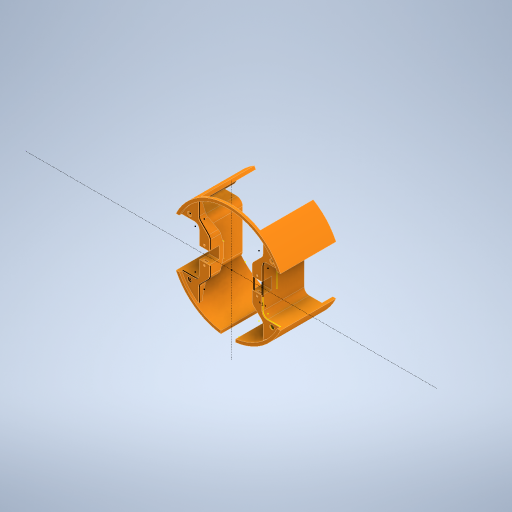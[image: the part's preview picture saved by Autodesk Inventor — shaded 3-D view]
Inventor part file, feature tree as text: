
AUTODESK INVENTOR PART (.ipt)
format: ipt  version: 2023.1 (Build 271208000, 208)  size: 742,400 bytes
history: native  units: mm
features: extrude x13, sketch x10, chamfer x6, projected_geometry x4, other x1, fillet x1, mirror x1
ambient origin geometry x8: Origin, YZ Plane, XZ Plane, XY Plane, X Axis, Y Axis, Z Axis, Center Point
bodies: Body1 (feature_tree)
feature tree (36):
  other  "Sólido1"
  extrude  "Extrusión1"  Depth=3.0mm
  extrude  "Extrusión2"  Depth=50.0mm
  extrude  "Extrusión3"  Depth=9.0mm
  fillet  "Empalme12"  Radius=15.0mm
  extrude  "Extrusión20"  Depth=2.5mm
  extrude  "Extrusión21"  Depth=7.0mm TaperAngle=0.0deg
  sketch  "Boceto16"  dims[d3=50.0mm d4=18.0mm]
  extrude  "Extrusión22"  Depth=5.0mm
  chamfer  "Chaflán3"  Distance=83.82mm
  chamfer  "Chaflán4"  Distance=26.04mm
  mirror  "Simetría6"
  chamfer  "Chaflán5"  Distance=1.079663mm
  chamfer  "Chaflán6"  [1 undecoded]
  chamfer  "Chaflán7"  Distance=10.0mm
  chamfer  "Chaflán8"  Distance=2.0mm
  extrude  "Extrusión24"  Depth=10.0mm
  extrude  "Extrusión25"  Depth=12.15mm
  sketch  "Boceto19"  dims[d13=1.0mm d14=0.0mm d15=7.0mm d16=0.0mm]
  extrude  "Extrusión26"  Depth=10.0mm
  extrude  "Extrusión28"  Depth=1.5mm
  extrude  "Extrusión29"  Depth=1.5mm
  sketch  "Boceto23"  dims[d116=110.0mm]
  sketch  "Boceto24"  dims[d117=41.91mm]
  extrude  "Extrusión30"  Depth=5.0mm
  extrude  "Extrusión31"  Depth=10.0mm TaperAngle=0.0deg
  sketch  "Boceto25"  dims[d119=57.92mm d120=83.82mm d121=26.04mm d131=1.079663mm d132=0.0mm d133=10.0mm d134=2.0mm d135=18.0mm d136=12.15mm d137=18.0mm d138=1.5mm d139=1.5mm d140=5.0mm d141=10.0mm d142=0.0mm d151=5.0mm d152=0.0mm d154=4.25mm d155=4.25mm d156=1.0mm d157=3.0mm d158=0.0mm d159=10.0mm d160=15.0mm d161=45.0deg d162=10.0mm d163=35.0mm d164=45.0deg d165=10.0mm d166=35.0mm d167=45.0deg d168=7.0mm d169=15.0mm d170=45.0deg d173=10.0mm d174=35.0mm d175=45.0deg d176=10.0mm d177=35.0mm d178=45.0deg d180=4.0mm d181=2.0mm d182=1.0mm d183=0.0mm d184=4.0mm d185=2.0mm d186=10.0mm d187=0.0mm d188=4.25mm d189=4.0mm d190=2.0mm d191=20.0mm d192=5.0mm d193=0.0mm d194=0.0mm d197=47.0mm d198=0.0mm d199=42.0mm d200=0.0mm d201=1.0mm d202=1.0mm d203=35.0mm d204=0.0mm d205=1.0mm d206=1.0mm d207=10.0mm d208=0.0mm d42=0.5mm d43=0.872665mm d44=0.5mm d45=0.872665mm d125=0.5mm d126=0.872665mm d127=0.5mm d128=0.872665mm]
  sketch  "Boceto15"  dims[d0=111.5mm d1=3.0mm]
  projected_geometry  "Contorno proyectado16"
  projected_geometry  "Contorno proyectado17"
  projected_geometry  "Contorno proyectado18"
  projected_geometry  "Contorno proyectado19"
  sketch  "Boceto17"  dims[d5=4.5mm d8=9.0mm d9=15.0mm]
  sketch  "Boceto18"  dims[d10=2.5mm d11=0.0mm d12=60.0mm]
  sketch  "Boceto20"  dims[d24=20.0mm d28=5.0mm]
  sketch  "Boceto22"  dims[d76=0.5mm]
note: 1 required parameter value undecoded (feature->parameter linkage not recoverable at this tier; creation-order binding heuristic only, values carry confidence <= 0.55)
